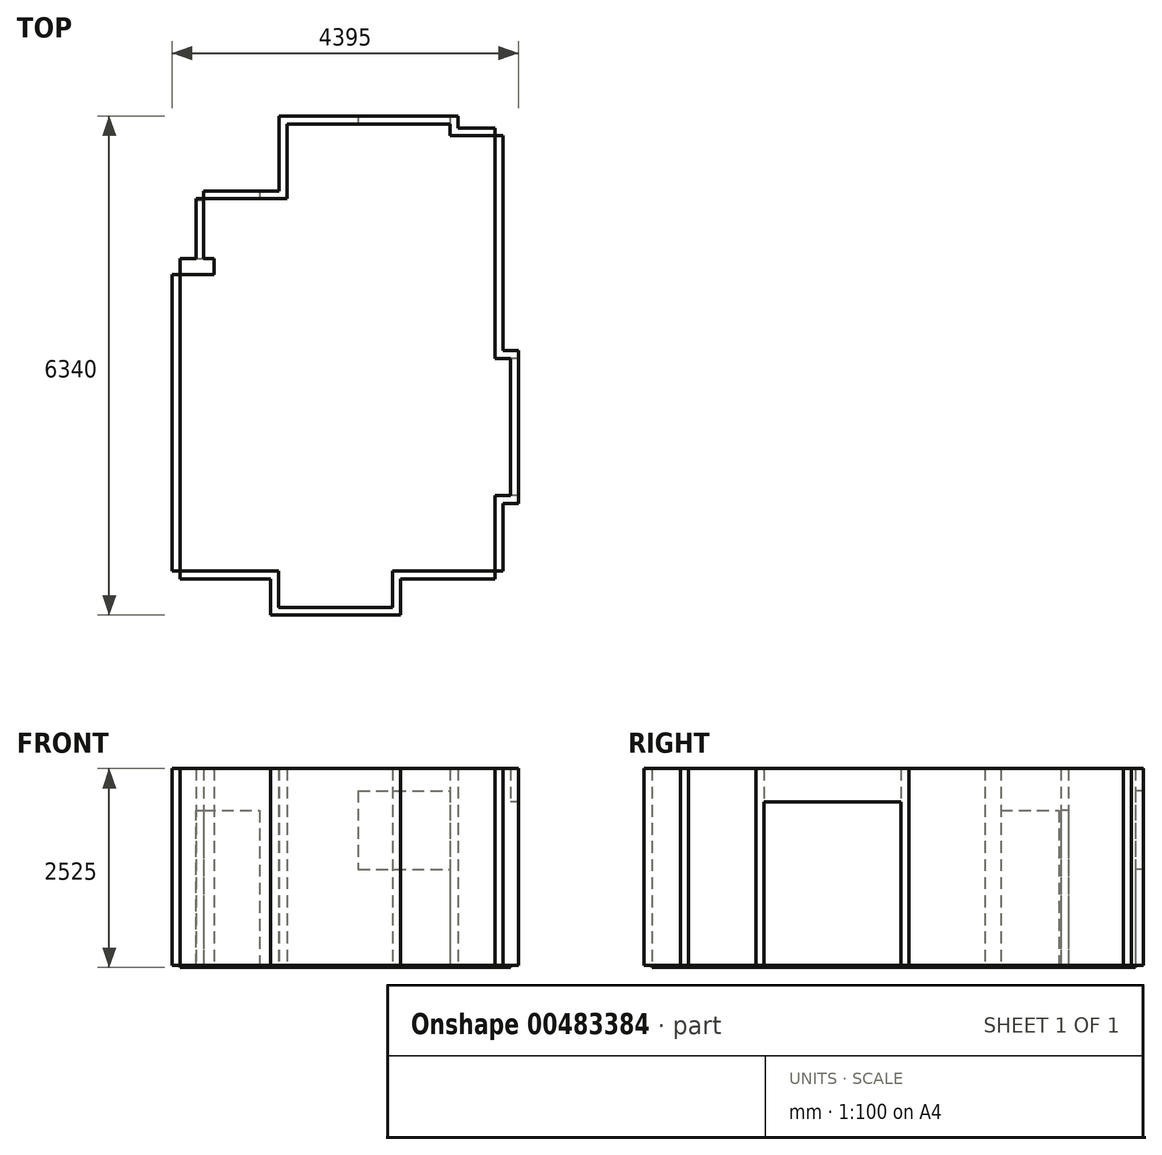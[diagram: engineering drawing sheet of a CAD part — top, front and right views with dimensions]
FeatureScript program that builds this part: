
annotation { "Feature Type Name" : "Feature", "Feature Type Description" : "" }
export const myFeature = defineFeature(function(context is Context, id is Id, definition is map)
    precondition{}
    {
        {
            var Q0;
            Q0=qCreatedBy(makeId("Top.planeOp"),FACE);
            var sketch = newSketch(context, id + "F0", { "sketchPlane" : qUnion([Q0])});
            skLineSegment(sketch, "E0", {"start": v(0, 0) * mm, "end": v(1250, 0) * mm});
            skLineSegment(sketch, "E1", {"start": v(1250, 0) * mm, "end": v(1250, -460) * mm});
            skLineSegment(sketch, "E2", {"start": v(1250, -460) * mm, "end": v(2700, -460) * mm});
            skLineSegment(sketch, "E3", {"start": v(2700, -460) * mm, "end": v(2700, 0) * mm});
            skLineSegment(sketch, "E4", {"start": v(2700, 0) * mm, "end": v(4000, 0) * mm});
            skLineSegment(sketch, "E5", {"start": v(4000, 0) * mm, "end": v(4000, 960) * mm});
            skLineSegment(sketch, "E6", {"start": v(4195, 960) * mm, "end": v(4000, 960) * mm});
            skLineSegment(sketch, "E7", {"start": v(4195, 960) * mm, "end": v(4195, 2700) * mm});
            skLineSegment(sketch, "E8", {"start": v(4195, 2700) * mm, "end": v(4000, 2700) * mm});
            skLineSegment(sketch, "E9", {"start": v(4000, 2700) * mm, "end": v(4000, 5530) * mm});
            skLineSegment(sketch, "E10.top", {"start": v(1360, 5680) * mm, "end": v(3430, 5680) * mm});
            skLineSegment(sketch, "E10.left", {"start": v(1360, 4730) * mm, "end": v(1360, 5680) * mm});
            skLineSegment(sketch, "E10.right", {"start": v(3430, 5530) * mm, "end": v(3430, 5680) * mm});
            skLineSegment(sketch, "E11", {"start": v(3430, 5530) * mm, "end": v(4000, 5530) * mm});
            skLineSegment(sketch, "E12", {"start": v(0, 0) * mm, "end": v(0, 3765) * mm});
            skLineSegment(sketch, "E13", {"start": v(0, 3765) * mm, "end": v(430, 3765) * mm});
            skLineSegment(sketch, "E14", {"start": v(430, 3765) * mm, "end": v(430, 3970) * mm});
            skLineSegment(sketch, "E15", {"start": v(430, 3970) * mm, "end": v(300, 3970) * mm});
            skLineSegment(sketch, "E16", {"start": v(1360, 4730) * mm, "end": v(300, 4730) * mm});
            skLineSegment(sketch, "E17", {"start": v(300, 4730) * mm, "end": v(300, 3970) * mm});
            skSolve(sketch);
        }
        {
            var Q0;
            Q0 = qSketchRegion(id + "F0", true);
            extrude(context, id + "F1", {"entities" : qUnion([Q0]), "oppositeDirection" : true, "depth" : 25 * mm});
        }
        {
            var Q0;
            Q0=makeQuery(id+"F1.opExtrude","CAP_FACE",FACE,{"disambiguationData":[OSD([sQuery(id+"F0.wireOp",EDGE,"E0"),sQuery(id+"F0.wireOp",EDGE,"E1"),sQuery(id+"F0.wireOp",EDGE,"E2"),sQuery(id+"F0.wireOp",EDGE,"E3"),sQuery(id+"F0.wireOp",EDGE,"E4"),sQuery(id+"F0.wireOp",EDGE,"E5"),sQuery(id+"F0.wireOp",EDGE,"E6"),sQuery(id+"F0.wireOp",EDGE,"E7"),sQuery(id+"F0.wireOp",EDGE,"E8"),sQuery(id+"F0.wireOp",EDGE,"E9"),sQuery(id+"F0.wireOp",EDGE,"E10.top"),sQuery(id+"F0.wireOp",EDGE,"E10.left"),sQuery(id+"F0.wireOp",EDGE,"E10.right"),sQuery(id+"F0.wireOp",EDGE,"E11"),sQuery(id+"F0.wireOp",EDGE,"E12"),sQuery(id+"F0.wireOp",EDGE,"E13"),sQuery(id+"F0.wireOp",EDGE,"E14"),sQuery(id+"F0.wireOp",EDGE,"E15"),sQuery(id+"F0.wireOp",EDGE,"E16"),sQuery(id+"F0.wireOp",EDGE,"E17")])],"isStart":true});
            var sketch = newSketch(context, id + "F2", { "sketchPlane" : qUnion([Q0])});
            skLineSegment(sketch, "E18.bottom", {"start": v(0, 0) * mm, "end": v(-100, 0) * mm});
            skLineSegment(sketch, "E18.top", {"start": v(0, 3765) * mm, "end": v(-100, 3765) * mm});
            skLineSegment(sketch, "E18.left", {"start": v(0, 0) * mm, "end": v(0, 3765) * mm});
            skLineSegment(sketch, "E18.right", {"start": v(-100, 0) * mm, "end": v(-100, 3765) * mm});
            skSolve(sketch);
        }
        {
            var Q0;
            Q0 = qSketchRegion(id + "F2", true);
            extrude(context, id + "F3", {"entities" : qUnion([Q0]), "depth" : 2500 * mm});
        }
        {
            var Q0;
            Q0=makeQuery(id+"F1.opExtrude","CAP_FACE",FACE,{"disambiguationData":[OSD([sQuery(id+"F0.wireOp",EDGE,"E0"),sQuery(id+"F0.wireOp",EDGE,"E1"),sQuery(id+"F0.wireOp",EDGE,"E2"),sQuery(id+"F0.wireOp",EDGE,"E3"),sQuery(id+"F0.wireOp",EDGE,"E4"),sQuery(id+"F0.wireOp",EDGE,"E5"),sQuery(id+"F0.wireOp",EDGE,"E6"),sQuery(id+"F0.wireOp",EDGE,"E7"),sQuery(id+"F0.wireOp",EDGE,"E8"),sQuery(id+"F0.wireOp",EDGE,"E9"),sQuery(id+"F0.wireOp",EDGE,"E10.top"),sQuery(id+"F0.wireOp",EDGE,"E10.left"),sQuery(id+"F0.wireOp",EDGE,"E10.right"),sQuery(id+"F0.wireOp",EDGE,"E11"),sQuery(id+"F0.wireOp",EDGE,"E12"),sQuery(id+"F0.wireOp",EDGE,"E13"),sQuery(id+"F0.wireOp",EDGE,"E14"),sQuery(id+"F0.wireOp",EDGE,"E15"),sQuery(id+"F0.wireOp",EDGE,"E16"),sQuery(id+"F0.wireOp",EDGE,"E17")])],"isStart":true});
            var sketch = newSketch(context, id + "F4", { "sketchPlane" : qUnion([Q0])});
            skLineSegment(sketch, "E19.right", {"start": v(0, 0) * mm, "end": v(0, -100) * mm});
            skLineSegment(sketch, "E20", {"start": v(0, -100) * mm, "end": v(1150, -100) * mm});
            skLineSegment(sketch, "E21", {"start": v(1250, 0) * mm, "end": v(0, 0) * mm});
            skLineSegment(sketch, "E22", {"start": v(1250, -460) * mm, "end": v(1250, 0) * mm});
            skLineSegment(sketch, "E23", {"start": v(2700, 0) * mm, "end": v(2700, -460) * mm});
            skLineSegment(sketch, "E24", {"start": v(2700, -460) * mm, "end": v(1250, -460) * mm});
            skLineSegment(sketch, "E25", {"start": v(1150, -560) * mm, "end": v(1150, -100) * mm});
            skLineSegment(sketch, "E26", {"start": v(2800, -560) * mm, "end": v(1150, -560) * mm});
            skLineSegment(sketch, "E27", {"start": v(4000, 0) * mm, "end": v(4000, -100) * mm});
            skLineSegment(sketch, "E28", {"start": v(4000, -100) * mm, "end": v(2800, -100) * mm});
            skLineSegment(sketch, "E29", {"start": v(2800, -100) * mm, "end": v(2800, -560) * mm});
            skSolve(sketch);
        }
        {
            var Q0;
            Q0 = qSketchRegion(id + "F4", true);
            var Q1;
            Q1=makeQuery(id+"F4.imprint","IMPRINT",FACE,{"disambiguationData":[TD([[makeQuery(id+"F4.imprint","IMPRINT",EDGE,{"derivedFrom":sQuery(id+"F4.wireOp",EDGE,"E19.right")}),1.0]])]});
            extrude(context, id + "F5", {"entities" : qUnion([Q0, Q1]), "depth" : 2500 * mm});
        }
        {
            var Q0;
            Q0=makeQuery(id+"F1.opExtrude","CAP_FACE",FACE,{"disambiguationData":[OSD([sQuery(id+"F0.wireOp",EDGE,"E0"),sQuery(id+"F0.wireOp",EDGE,"E1"),sQuery(id+"F0.wireOp",EDGE,"E2"),sQuery(id+"F0.wireOp",EDGE,"E3"),sQuery(id+"F0.wireOp",EDGE,"E4"),sQuery(id+"F0.wireOp",EDGE,"E5"),sQuery(id+"F0.wireOp",EDGE,"E6"),sQuery(id+"F0.wireOp",EDGE,"E7"),sQuery(id+"F0.wireOp",EDGE,"E8"),sQuery(id+"F0.wireOp",EDGE,"E9"),sQuery(id+"F0.wireOp",EDGE,"E10.top"),sQuery(id+"F0.wireOp",EDGE,"E10.left"),sQuery(id+"F0.wireOp",EDGE,"E10.right"),sQuery(id+"F0.wireOp",EDGE,"E11"),sQuery(id+"F0.wireOp",EDGE,"E12"),sQuery(id+"F0.wireOp",EDGE,"E13"),sQuery(id+"F0.wireOp",EDGE,"E14"),sQuery(id+"F0.wireOp",EDGE,"E15"),sQuery(id+"F0.wireOp",EDGE,"E16"),sQuery(id+"F0.wireOp",EDGE,"E17")])],"isStart":true});
            var sketch = newSketch(context, id + "F6", { "sketchPlane" : qUnion([Q0])});
            skLineSegment(sketch, "E30", {"start": v(4000, 0) * mm, "end": v(4100, 0) * mm});
            skLineSegment(sketch, "E31", {"start": v(4100, 0) * mm, "end": v(4100, 860) * mm});
            skLineSegment(sketch, "E32", {"start": v(4100, 860) * mm, "end": v(4295, 860) * mm});
            skLineSegment(sketch, "E33", {"start": v(4295, 860) * mm, "end": v(4295, 2800) * mm});
            skLineSegment(sketch, "E34", {"start": v(4295, 2800) * mm, "end": v(4100, 2800) * mm});
            skLineSegment(sketch, "E35", {"start": v(4100, 2800) * mm, "end": v(4100, 5530) * mm});
            skLineSegment(sketch, "E36", {"start": v(4100, 5530) * mm, "end": v(4000, 5530) * mm});
            skLineSegment(sketch, "E37", {"start": v(4000, 5530) * mm, "end": v(4000, 2700) * mm});
            skLineSegment(sketch, "E38", {"start": v(4000, 2700) * mm, "end": v(4195, 2700) * mm});
            skLineSegment(sketch, "E39", {"start": v(4195, 2700) * mm, "end": v(4195, 960) * mm});
            skLineSegment(sketch, "E40", {"start": v(4195, 960) * mm, "end": v(4000, 960) * mm});
            skLineSegment(sketch, "E41", {"start": v(4000, 960) * mm, "end": v(4000, 0) * mm});
            skSolve(sketch);
        }
        {
            var Q0;
            Q0 = qSketchRegion(id + "F6", true);
            extrude(context, id + "F7", {"entities" : qUnion([Q0]), "depth" : 2500 * mm});
        }
        {
            var Q0;
            Q0=makeQuery(id+"F1.opExtrude","CAP_FACE",FACE,{"disambiguationData":[OSD([sQuery(id+"F0.wireOp",EDGE,"E0"),sQuery(id+"F0.wireOp",EDGE,"E1"),sQuery(id+"F0.wireOp",EDGE,"E2"),sQuery(id+"F0.wireOp",EDGE,"E3"),sQuery(id+"F0.wireOp",EDGE,"E4"),sQuery(id+"F0.wireOp",EDGE,"E5"),sQuery(id+"F0.wireOp",EDGE,"E6"),sQuery(id+"F0.wireOp",EDGE,"E7"),sQuery(id+"F0.wireOp",EDGE,"E8"),sQuery(id+"F0.wireOp",EDGE,"E9"),sQuery(id+"F0.wireOp",EDGE,"E10.top"),sQuery(id+"F0.wireOp",EDGE,"E10.left"),sQuery(id+"F0.wireOp",EDGE,"E10.right"),sQuery(id+"F0.wireOp",EDGE,"E11"),sQuery(id+"F0.wireOp",EDGE,"E12"),sQuery(id+"F0.wireOp",EDGE,"E13"),sQuery(id+"F0.wireOp",EDGE,"E14"),sQuery(id+"F0.wireOp",EDGE,"E15"),sQuery(id+"F0.wireOp",EDGE,"E16"),sQuery(id+"F0.wireOp",EDGE,"E17")])],"isStart":true});
            var sketch = newSketch(context, id + "F8", { "sketchPlane" : qUnion([Q0])});
            skLineSegment(sketch, "E42", {"start": v(430, 3765) * mm, "end": v(430, 3970) * mm});
            skLineSegment(sketch, "E43", {"start": v(430, 3970) * mm, "end": v(0, 3970) * mm});
            skLineSegment(sketch, "E44", {"start": v(0, 3765) * mm, "end": v(0, 3970) * mm});
            skSolve(sketch);
        }
        {
            var Q0;
            {var subQ3=sQuery(id+"F8.wireOp",EDGE,"E42");Q0=makeQuery(id+"F8.imprint","IMPRINT",FACE,{"disambiguationData":[TD([[makeQuery(id+"F8.imprint","IMPRINT",EDGE,{"derivedFrom":subQ3}),1.0]])]});}
            extrude(context, id + "F9", {"entities" : qUnion([Q0]), "depth" : 2500 * mm});
        }
        {
            var Q0;
            Q0=makeQuery(id+"F1.opExtrude","CAP_FACE",FACE,{"disambiguationData":[OSD([sQuery(id+"F0.wireOp",EDGE,"E0"),sQuery(id+"F0.wireOp",EDGE,"E1"),sQuery(id+"F0.wireOp",EDGE,"E2"),sQuery(id+"F0.wireOp",EDGE,"E3"),sQuery(id+"F0.wireOp",EDGE,"E4"),sQuery(id+"F0.wireOp",EDGE,"E5"),sQuery(id+"F0.wireOp",EDGE,"E6"),sQuery(id+"F0.wireOp",EDGE,"E7"),sQuery(id+"F0.wireOp",EDGE,"E8"),sQuery(id+"F0.wireOp",EDGE,"E9"),sQuery(id+"F0.wireOp",EDGE,"E10.top"),sQuery(id+"F0.wireOp",EDGE,"E10.left"),sQuery(id+"F0.wireOp",EDGE,"E10.right"),sQuery(id+"F0.wireOp",EDGE,"E11"),sQuery(id+"F0.wireOp",EDGE,"E12"),sQuery(id+"F0.wireOp",EDGE,"E13"),sQuery(id+"F0.wireOp",EDGE,"E14"),sQuery(id+"F0.wireOp",EDGE,"E15"),sQuery(id+"F0.wireOp",EDGE,"E16"),sQuery(id+"F0.wireOp",EDGE,"E17")])],"isStart":true});
            var sketch = newSketch(context, id + "F10", { "sketchPlane" : qUnion([Q0])});
            skLineSegment(sketch, "E45", {"start": v(4000, 5530) * mm, "end": v(4000, 5630) * mm});
            skLineSegment(sketch, "E46", {"start": v(4000, 5630) * mm, "end": v(3530, 5630) * mm});
            skLineSegment(sketch, "E47", {"start": v(3530, 5630) * mm, "end": v(3530, 5780) * mm});
            skLineSegment(sketch, "E48", {"start": v(3530, 5780) * mm, "end": v(1260, 5780) * mm});
            skLineSegment(sketch, "E49", {"start": v(1260, 5780) * mm, "end": v(1260, 4830) * mm});
            skLineSegment(sketch, "E50", {"start": v(1260, 4830) * mm, "end": v(300, 4830) * mm});
            skLineSegment(sketch, "E51", {"start": v(300, 4730) * mm, "end": v(300, 4830) * mm});
            skSolve(sketch);
        }
        {
            var Q0;
            Q0=makeQuery(id+"F10.imprint","IMPRINT",FACE,{"disambiguationData":[TD([[makeQuery(id+"F10.imprint","IMPRINT",EDGE,{"derivedFrom":sQuery(id+"F10.wireOp",EDGE,"E45")}),1.0]])]});
            extrude(context, id + "F11", {"entities" : qUnion([Q0]), "depth" : 2500 * mm});
        }
        {
            var Q0;
            Q0=makeQuery(id+"F1.opExtrude","CAP_FACE",FACE,{"disambiguationData":[OSD([sQuery(id+"F0.wireOp",EDGE,"E0"),sQuery(id+"F0.wireOp",EDGE,"E1"),sQuery(id+"F0.wireOp",EDGE,"E2"),sQuery(id+"F0.wireOp",EDGE,"E3"),sQuery(id+"F0.wireOp",EDGE,"E4"),sQuery(id+"F0.wireOp",EDGE,"E5"),sQuery(id+"F0.wireOp",EDGE,"E6"),sQuery(id+"F0.wireOp",EDGE,"E7"),sQuery(id+"F0.wireOp",EDGE,"E8"),sQuery(id+"F0.wireOp",EDGE,"E9"),sQuery(id+"F0.wireOp",EDGE,"E10.top"),sQuery(id+"F0.wireOp",EDGE,"E10.left"),sQuery(id+"F0.wireOp",EDGE,"E10.right"),sQuery(id+"F0.wireOp",EDGE,"E11"),sQuery(id+"F0.wireOp",EDGE,"E12"),sQuery(id+"F0.wireOp",EDGE,"E13"),sQuery(id+"F0.wireOp",EDGE,"E14"),sQuery(id+"F0.wireOp",EDGE,"E15"),sQuery(id+"F0.wireOp",EDGE,"E16"),sQuery(id+"F0.wireOp",EDGE,"E17")])],"isStart":true});
            var sketch = newSketch(context, id + "F12", { "sketchPlane" : qUnion([Q0])});
            skLineSegment(sketch, "E52", {"start": v(300, 3970) * mm, "end": v(200, 3970) * mm});
            skLineSegment(sketch, "E53", {"start": v(200, 3970) * mm, "end": v(200, 4730) * mm});
            skLineSegment(sketch, "E54", {"start": v(200, 4730) * mm, "end": v(300, 4730) * mm});
            skLineSegment(sketch, "E55", {"start": v(300, 4730) * mm, "end": v(300, 3970) * mm});
            skSolve(sketch);
        }
        {
            var Q0;
            Q0=makeQuery(id+"F12.imprint","IMPRINT",FACE,{"disambiguationData":[TD([[makeQuery(id+"F12.imprint","IMPRINT",EDGE,{"derivedFrom":sQuery(id+"F12.wireOp",EDGE,"E52")}),-1.0]])]});
            extrude(context, id + "F13", {"entities" : qUnion([Q0]), "operationType" : NewBodyOperationType.ADD, "depth" : 2500 * mm});
        }
        {
            var Q0;
            Q0=makeQuery(id+"F11.opExtrude","SWEPT_FACE",FACE,{"disambiguationData":[OSD([sQuery(id+"F0.wireOp",EDGE,"E10.top")])]});
            var sketch = newSketch(context, id + "F14", { "sketchPlane" : qUnion([Q0])});
            skLineSegment(sketch, "E56.bottom", {"start": v(2260, 2220) * mm, "end": v(3430, 2220) * mm});
            skLineSegment(sketch, "E56.top", {"start": v(2260, 1220) * mm, "end": v(3430, 1220) * mm});
            skLineSegment(sketch, "E56.left", {"start": v(2260, 2220) * mm, "end": v(2260, 1220) * mm});
            skLineSegment(sketch, "E56.right", {"start": v(3430, 2220) * mm, "end": v(3430, 1220) * mm});
            skSolve(sketch);
        }
        {
            var Q0;
            Q0 = qSketchRegion(id + "F14", true);
            extrude(context, id + "F15", {"entities" : qUnion([Q0]), "operationType" : NewBodyOperationType.REMOVE, "endBound" : BoundingType.THROUGH_ALL, "oppositeDirection" : true, "depth" : 25 * mm});
        }
        {
            var Q0;
            Q0=makeQuery(id+"F13.opExtrude","SWEPT_FACE",FACE,{"disambiguationData":[OSD([sQuery(id+"F12.wireOp",EDGE,"E55")])]});
            var sketch = newSketch(context, id + "F16", { "sketchPlane" : qUnion([Q0])});
            skLineSegment(sketch, "E57.bottom", {"start": v(3970, 1970) * mm, "end": v(4710, 1970) * mm});
            skLineSegment(sketch, "E57.top", {"start": v(3970, 0) * mm, "end": v(4710, 0) * mm});
            skLineSegment(sketch, "E57.left", {"start": v(3970, 1970) * mm, "end": v(3970, 0) * mm});
            skLineSegment(sketch, "E57.right", {"start": v(4710, 1970) * mm, "end": v(4710, 0) * mm});
            skSolve(sketch);
        }
        {
            var Q0;
            Q0 = qSketchRegion(id + "F16", true);
            extrude(context, id + "F17", {"entities" : qUnion([Q0]), "operationType" : NewBodyOperationType.REMOVE, "endBound" : BoundingType.THROUGH_ALL, "oppositeDirection" : true, "depth" : 25 * mm});
        }
        {
            var Q0;
            Q0=makeQuery(id+"F11.opExtrude","SWEPT_FACE",FACE,{"disambiguationData":[OSD([sQuery(id+"F0.wireOp",EDGE,"E16")])]});
            var sketch = newSketch(context, id + "F18", { "sketchPlane" : qUnion([Q0])});
            skLineSegment(sketch, "E58.bottom", {"start": v(300, 1970) * mm, "end": v(1010, 1970) * mm});
            skLineSegment(sketch, "E58.top", {"start": v(300, 0) * mm, "end": v(1010, 0) * mm});
            skLineSegment(sketch, "E58.left", {"start": v(300, 1970) * mm, "end": v(300, 0) * mm});
            skLineSegment(sketch, "E58.right", {"start": v(1010, 1970) * mm, "end": v(1010, 0) * mm});
            skSolve(sketch);
        }
        {
            var Q0;
            Q0 = qSketchRegion(id + "F18", true);
            extrude(context, id + "F19", {"entities" : qUnion([Q0]), "operationType" : NewBodyOperationType.REMOVE, "endBound" : BoundingType.THROUGH_ALL, "oppositeDirection" : true, "depth" : 25 * mm});
        }
        {
            var Q0;
            Q0=makeQuery(id+"F7.opExtrude","SWEPT_FACE",FACE,{"disambiguationData":[OSD([sQuery(id+"F6.wireOp",EDGE,"E39")])]});
            var sketch = newSketch(context, id + "F20", { "sketchPlane" : qUnion([Q0])});
            skLineSegment(sketch, "E59.bottom", {"start": v(-2700, 2080) * mm, "end": v(-960, 2080) * mm});
            skLineSegment(sketch, "E59.top", {"start": v(-2700, 0) * mm, "end": v(-960, 0) * mm});
            skLineSegment(sketch, "E59.left", {"start": v(-2700, 2080) * mm, "end": v(-2700, 0) * mm});
            skLineSegment(sketch, "E59.right", {"start": v(-960, 2080) * mm, "end": v(-960, 0) * mm});
            skSolve(sketch);
        }
        {
            var Q0;
            Q0 = qSketchRegion(id + "F20", true);
            extrude(context, id + "F21", {"entities" : qUnion([Q0]), "operationType" : NewBodyOperationType.REMOVE, "endBound" : BoundingType.THROUGH_ALL, "oppositeDirection" : true, "depth" : 25 * mm});
        }
    });
